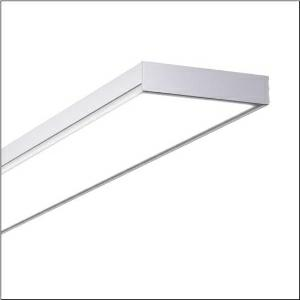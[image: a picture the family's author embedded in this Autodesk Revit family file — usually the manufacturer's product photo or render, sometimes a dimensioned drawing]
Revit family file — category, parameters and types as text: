
# Revit family: apollon_r__31_surface_51mp26wd2441ea_40fe
name_source: partatom
category: Lighting Fixtures
units: mm (PartAtom-declared; Revit-internal decimal feet)

## family parameters
Cut with Voids When Loaded = No
Host = Face
Light Source = No
Part Type = Normal
Room Calculation Point = No
Round Connector Dimension = Use Diameter
Shared = No

## types (1)
- Apollon® 31 Surface (1 x LED, 4600 lm, 33 W, 4000K)
    Apparent Load = 33 VA
    CIE Flux Codes = 61 87 97 97 100
    Color Rendering = 80
    Color Temperature = 4000K
    Default Elevation = 1800 mm
    Description = Apollon® 31 Surface, office luminaire, primary optical cover: micro prismatic cover, of PMMA, light emission: direct distribution, primary light characteristic: symmetric, installation type: surface-mounted, LED, rated luminous flux: 4.600lm, luminous efficacy: 139lm/W, light colour: 840, colour temperature: 4000K, control gear: DALI 2, with terminal, 5-pole, mains connection: 220..240V, AC, 50/60Hz, rated input power: 33W, housing, of sheet steel, coil coated, metallic grey (RAL 9006), length: 1.545mm, width: 200mm, height: 44mm, protection rating (complete): IP20, insulation class (complete): insulation class II (safety insulation), certification: CE, impact resistance: IK02, permissible operating ambient temperature: -20..+40°C, standard: EN 60598-2-22, packaging unit: 1 piece
    Height = 44 mm
    Lamp = 1 x LED
    Lamp Light Flux = 4600 lm
    Lamp Power = 33 W
    Lamp count = 1
    Length = 1545 mm
    Luminous efficacy = 139 lm/W
    Manufacturer = Siteco
    ModVariant = No
    Model = 51MP26WD2441EA
    Mounting Place = Ceiling
    Mounting Type = Surface mounted
    Number of Poles = 1
    OnlyDefault = Yes
    Power Factor = 1
    Product Name = Apollon® 31 Surface
    Product group = office luminaire | ceiling mounted
    ProductGroupID = 303
    Protection Class = Protection class II
    Protection Degree = IP 20
    RLX_Detail_Level = 1
    RLX_Emergency_Light_Flux = 0 lm
    RLX_Emergency_Type = 0
    RLX_Emergency_Type_DB = No
    RlxData = <blob elided: 24129 chars, md5=831781c4>
    Socket = socket
    Standby Power = 0 W
    System Light Flux = 4600 lm
    System Power = 33 W
    Type Comments = Product without accessories
    Type Image = l_1313654.jpg
    URL = http://relux.com
    VarID = ---
    Voltage = 0 V
    Weight = 0.00 kg
    Width = 200 mm  [stored 0.656168 ft]

note: [stored X ft] marks values corroborated as IEEE doubles in the binary element streams (Revit-internal decimal feet)

## geometry (parser evidence)
native form markers: Blend x4, Sweep x11
no freeform markers — native parametric forms only
